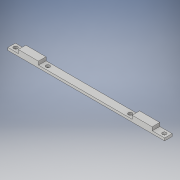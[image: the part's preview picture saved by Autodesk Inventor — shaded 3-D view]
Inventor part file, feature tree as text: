
AUTODESK INVENTOR PART (.ipt)
format: ipt  version: 2018 (Build 220112000, 112)  size: 136,192 bytes
history: native  units: in
note: dims shown in document units (in); Inventor stores cm internally (conversion verified against a paired STEP export)
features: extrude x2, sketch x2, fillet x1
ambient origin geometry x8: Origin, YZ Plane, XZ Plane, XY Plane, X Axis, Y Axis, Z Axis, Center Point
bodies: Solid1 (feature_tree)
feature tree (5):
  extrude  "Extrusion1"  Depth=0.1181in
  extrude  "Extrusion2"  Depth=0.2362in
  fillet  "Fillet1"  Radius=0.1181in
  sketch  "Sketch1"  dims[d0=2.5787in d1=0.1181in]
  sketch  "Sketch2"  dims[d2=0.1181in d3=0.2362in d7=0.1181in d8=0.1181in d9=0.0787in d10=0.0in d17=4.909in d18=0.125in d19=0.125in d20=0.1772in d21=0.6299in d22=0.1772in d23=0.6299in d24=0.1083in d25=0.0in d26=0.0787in]
